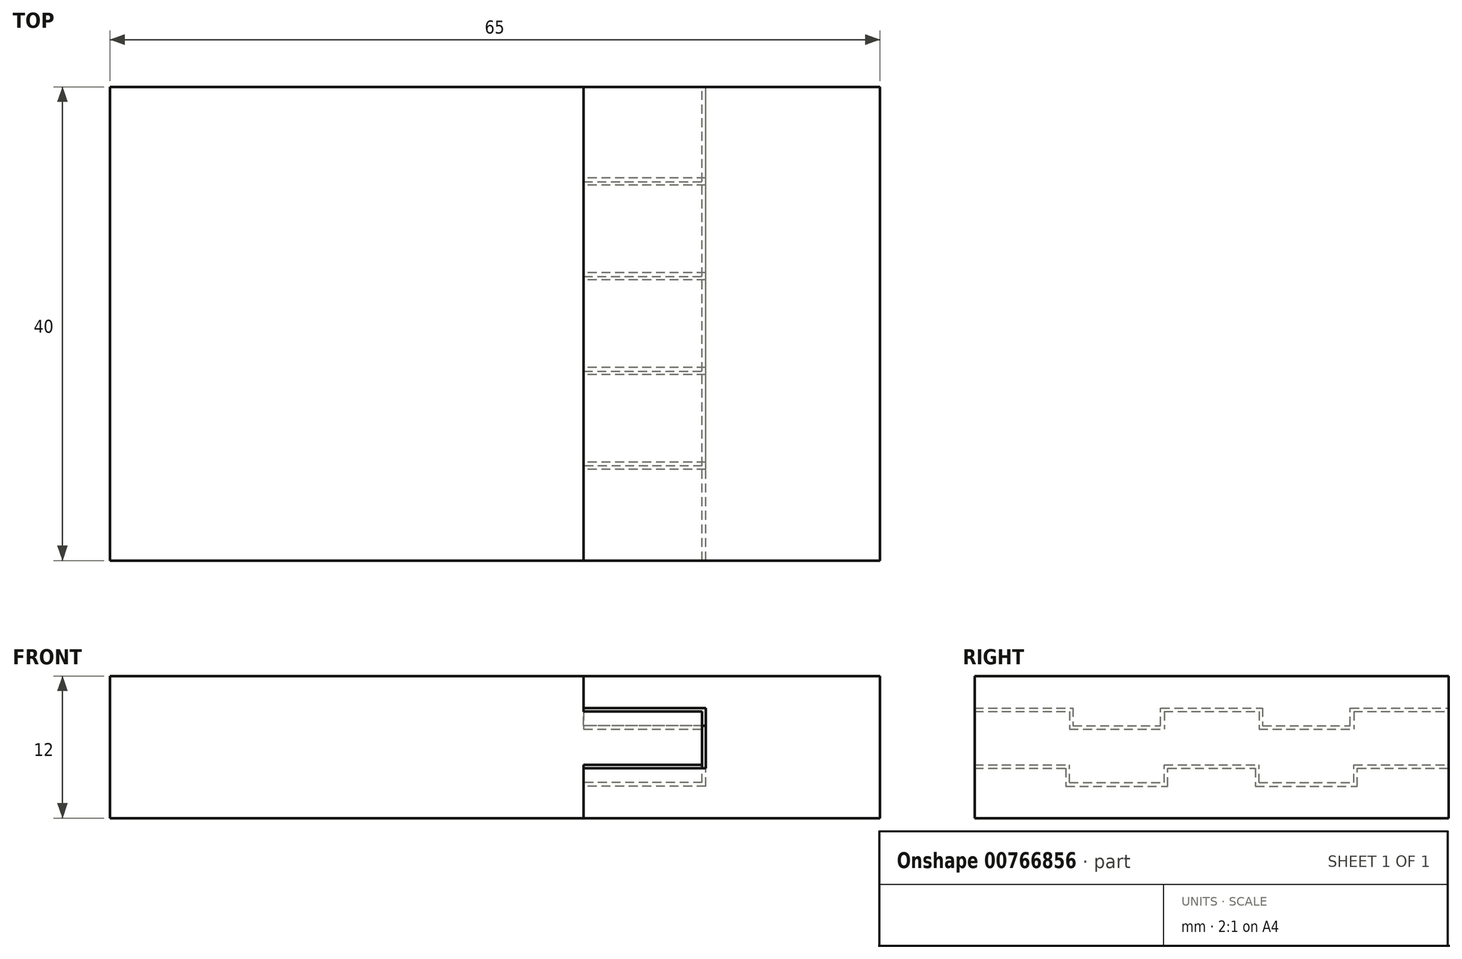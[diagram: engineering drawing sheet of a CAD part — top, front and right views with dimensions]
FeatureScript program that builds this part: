
annotation { "Feature Type Name" : "Feature", "Feature Type Description" : "" }
export const myFeature = defineFeature(function(context is Context, id is Id, definition is map)
    precondition{}
    {
        {
            var Q0;
            Q0=qCreatedBy(makeId("Top.planeOp"),FACE);
            var sketch = newSketch(context, id + "F0", { "sketchPlane" : qUnion([Q0])});
            skLineSegment(sketch, "E0.bottom", {"start": v(-40, 40) * mm, "end": v(0, 40) * mm});
            skLineSegment(sketch, "E0.top", {"start": v(-40, 0) * mm, "end": v(0, 0) * mm});
            skLineSegment(sketch, "E0.left", {"start": v(-40, 40) * mm, "end": v(-40, 0) * mm});
            skLineSegment(sketch, "E1", {"start": v(0, 0) * mm, "end": v(0, 40) * mm});
            skLineSegment(sketch, "E2.bottom", {"start": v(0, 0) * mm, "end": v(10, 0) * mm});
            skLineSegment(sketch, "E2.top", {"start": v(0, 8) * mm, "end": v(10, 8) * mm});
            skLineSegment(sketch, "E2.left", {"start": v(0, 0) * mm, "end": v(0, 8) * mm});
            skLineSegment(sketch, "E2.right", {"start": v(10, 0) * mm, "end": v(10, 8) * mm});
            skLineSegment(sketch, "E3.bottom", {"start": v(10, 8) * mm, "end": v(0, 8) * mm});
            skLineSegment(sketch, "E3.top", {"start": v(10, 16) * mm, "end": v(0, 16) * mm});
            skLineSegment(sketch, "E3.left", {"start": v(10, 8) * mm, "end": v(10, 16) * mm});
            skLineSegment(sketch, "E3.right", {"start": v(0, 8) * mm, "end": v(0, 16) * mm});
            skLineSegment(sketch, "E4.top", {"start": v(10, 24) * mm, "end": v(0, 24) * mm});
            skLineSegment(sketch, "E4.left", {"start": v(10, 16) * mm, "end": v(10, 24) * mm});
            skLineSegment(sketch, "E4.right", {"start": v(0, 16) * mm, "end": v(0, 24) * mm});
            skLineSegment(sketch, "E5.top", {"start": v(10, 32) * mm, "end": v(0, 32) * mm});
            skLineSegment(sketch, "E5.left", {"start": v(10, 24) * mm, "end": v(10, 32) * mm});
            skLineSegment(sketch, "E5.right", {"start": v(0, 24) * mm, "end": v(0, 32) * mm});
            skLineSegment(sketch, "E6.top", {"start": v(10, 40) * mm, "end": v(0, 40) * mm});
            skLineSegment(sketch, "E6.left", {"start": v(10, 32) * mm, "end": v(10, 40) * mm});
            skLineSegment(sketch, "E6.right", {"start": v(0, 32) * mm, "end": v(0, 40) * mm});
            skSolve(sketch);
        }
        {
            var Q0;
            {var subQ4=sQuery(id+"F0.wireOp",EDGE,"E0.bottom");Q0=makeQuery(id+"F0.imprint","IMPRINT",FACE,{"disambiguationData":[TD([[makeQuery(id+"F0.imprint","IMPRINT",EDGE,{"derivedFrom":subQ4}),-1.0]])]});}
            extrude(context, id + "F1", {"entities" : qUnion([Q0]), "endBound" : BoundingType.SYMMETRIC, "depth" : 12 * mm, "offsetDistance" : 25 * mm});
        }
        {
            var Q0;
            {var subQ0=sQuery(id+"F0.wireOp",EDGE,"E2.bottom");Q0=makeQuery(id+"F0.imprint","IMPRINT",FACE,{"disambiguationData":[TD([[makeQuery(id+"F0.imprint","IMPRINT",EDGE,{"derivedFrom":subQ0}),1.0]])]});}
            var Q1;
            {var subQ0=sQuery(id+"F0.wireOp",EDGE,"E3.top");Q1=makeQuery(id+"F0.imprint","IMPRINT",FACE,{"disambiguationData":[TD([[makeQuery(id+"F0.imprint","IMPRINT",EDGE,{"derivedFrom":subQ0}),-1.0]])]});}
            var Q2;
            {var subQ0=sQuery(id+"F0.wireOp",EDGE,"E2.top");Q2=makeQuery(id+"F0.imprint","IMPRINT",FACE,{"disambiguationData":[TD([[makeQuery(id+"F0.imprint","IMPRINT",EDGE,{"derivedFrom":subQ0}),1.0]])]});}
            var Q3;
            {var subQ0=sQuery(id+"F0.wireOp",EDGE,"E4.top");Q3=makeQuery(id+"F0.imprint","IMPRINT",FACE,{"disambiguationData":[TD([[makeQuery(id+"F0.imprint","IMPRINT",EDGE,{"derivedFrom":subQ0}),-1.0]])]});}
            var Q4;
            {var subQ2=sQuery(id+"F0.wireOp",EDGE,"E5.top");Q4=makeQuery(id+"F0.imprint","IMPRINT",FACE,{"disambiguationData":[TD([[makeQuery(id+"F0.imprint","IMPRINT",EDGE,{"derivedFrom":subQ2}),-1.0]])]});}
            extrude(context, id + "F2", {"entities" : qUnion([Q0, Q1, Q2, Q3, Q4]), "operationType" : NewBodyOperationType.ADD, "endBound" : BoundingType.SYMMETRIC, "depth" : 3 * mm, "offsetDistance" : 25 * mm});
        }
        {
            var Q0;
            {var subQ0=sQuery(id+"F0.wireOp",EDGE,"E2.bottom");Q0=makeQuery(id+"F0.imprint","IMPRINT",FACE,{"disambiguationData":[TD([[makeQuery(id+"F0.imprint","IMPRINT",EDGE,{"derivedFrom":subQ0}),1.0]])]});}
            var Q1;
            {var subQ0=sQuery(id+"F0.wireOp",EDGE,"E3.top");Q1=makeQuery(id+"F0.imprint","IMPRINT",FACE,{"disambiguationData":[TD([[makeQuery(id+"F0.imprint","IMPRINT",EDGE,{"derivedFrom":subQ0}),-1.0]])]});}
            var Q2;
            {var subQ2=sQuery(id+"F0.wireOp",EDGE,"E5.top");Q2=makeQuery(id+"F0.imprint","IMPRINT",FACE,{"disambiguationData":[TD([[makeQuery(id+"F0.imprint","IMPRINT",EDGE,{"derivedFrom":subQ2}),-1.0]])]});}
            extrude(context, id + "F3", {"entities" : qUnion([Q0, Q1, Q2]), "operationType" : NewBodyOperationType.ADD, "depth" : 3 * mm, "offsetDistance" : 25 * mm});
        }
        {
            var Q0;
            {var subQ0=sQuery(id+"F0.wireOp",EDGE,"E2.right");var subQ1=sQuery(id+"F0.wireOp",EDGE,"E6.left");var subQ2=sQuery(id+"F0.wireOp",EDGE,"E5.left");var subQ3=sQuery(id+"F0.wireOp",EDGE,"E4.left");var subQ4=sQuery(id+"F0.wireOp",EDGE,"E3.left");var subQ5=sQuery(id+"F0.wireOp",EDGE,"E1");Q0=makeQuery(id+"F3.boolean.opBoolean","SPLIT",FACE,{"disambiguationData":[TD([makeQuery(id+"F3.opExtrude","SWEPT_FACE",FACE,{"disambiguationData":[OSD([sQuery(id+"F0.wireOp",EDGE,"E2.top")])]})])],"derivedFrom":makeQuery(id+"F2.opExtrude","CAP_FACE",FACE,{"disambiguationData":[OSD([subQ5,sQuery(id+"F0.wireOp",EDGE,"E2.bottom"),subQ0,subQ4,subQ3,subQ2,sQuery(id+"F0.wireOp",EDGE,"E6.top"),subQ1])],"isStart":false})});}
            var Q1;
            {var subQ0=sQuery(id+"F0.wireOp",EDGE,"E2.right");var subQ1=sQuery(id+"F0.wireOp",EDGE,"E6.left");var subQ2=sQuery(id+"F0.wireOp",EDGE,"E5.left");var subQ3=sQuery(id+"F0.wireOp",EDGE,"E4.left");var subQ4=sQuery(id+"F0.wireOp",EDGE,"E3.left");var subQ5=sQuery(id+"F0.wireOp",EDGE,"E1");Q1=makeQuery(id+"F3.boolean.opBoolean","SPLIT",FACE,{"disambiguationData":[TD([makeQuery(id+"F3.opExtrude","SWEPT_FACE",FACE,{"disambiguationData":[OSD([sQuery(id+"F0.wireOp",EDGE,"E4.top")])]})])],"derivedFrom":makeQuery(id+"F2.opExtrude","CAP_FACE",FACE,{"disambiguationData":[OSD([subQ5,sQuery(id+"F0.wireOp",EDGE,"E2.bottom"),subQ0,subQ4,subQ3,subQ2,sQuery(id+"F0.wireOp",EDGE,"E6.top"),subQ1])],"isStart":false})});}
            extrude(context, id + "F4", {"entities" : qUnion([Q0, Q1]), "operationType" : NewBodyOperationType.ADD, "oppositeDirection" : true, "depth" : 4.5 * mm, "offsetDistance" : 25 * mm});
        }
        {
            var Q0;
            {var subQ2=sQuery(id+"F0.wireOp",EDGE,"E1");var subQ3=sQuery(id+"F0.wireOp",EDGE,"E0.top");var subQ4=sQuery(id+"F0.wireOp",EDGE,"E0.bottom");Q0=makeQuery(id+"F2.boolean.opBoolean","SPLIT",FACE,{"disambiguationData":[TD([makeQuery(id+"F1.opExtrude","CAP_FACE",FACE,{"disambiguationData":[OSD([subQ4,subQ3,sQuery(id+"F0.wireOp",EDGE,"E0.left"),subQ2])],"isStart":false})])],"derivedFrom":makeQuery(id+"F1.opExtrude","SWEPT_FACE",FACE,{"disambiguationData":[OSD([subQ2])]})});}
            var sketch = newSketch(context, id + "F5", { "sketchPlane" : qUnion([Q0])});
            skLineSegment(sketch, "E7.0.0", {"start": v(32, 1.5) * mm, "end": v(32, 3) * mm});
            skLineSegment(sketch, "E7.0.1", {"start": v(32, 3) * mm, "end": v(40, 3) * mm});
            skLineSegment(sketch, "E7.0.2", {"start": v(40, 3) * mm, "end": v(40, 6) * mm});
            skLineSegment(sketch, "E7.0.3", {"start": v(40, 6) * mm, "end": v(0, 6) * mm});
            skLineSegment(sketch, "E7.0.4", {"start": v(0, 6) * mm, "end": v(0, 3) * mm});
            skLineSegment(sketch, "E7.0.5", {"start": v(0, 3) * mm, "end": v(8, 3) * mm});
            skLineSegment(sketch, "E7.0.6", {"start": v(8, 3) * mm, "end": v(8, 1.5) * mm});
            skLineSegment(sketch, "E7.0.7", {"start": v(8, 1.5) * mm, "end": v(16, 1.5) * mm});
            skLineSegment(sketch, "E7.0.8", {"start": v(16, 1.5) * mm, "end": v(16, 3) * mm});
            skLineSegment(sketch, "E7.0.9", {"start": v(16, 3) * mm, "end": v(24, 3) * mm});
            skLineSegment(sketch, "E7.0.10", {"start": v(24, 3) * mm, "end": v(24, 1.5) * mm});
            skLineSegment(sketch, "E7.0.11", {"start": v(24, 1.5) * mm, "end": v(32, 1.5) * mm});
            skLineSegment(sketch, "E8.0.0", {"start": v(32, -1.5) * mm, "end": v(32, -3) * mm});
            skLineSegment(sketch, "E8.0.1", {"start": v(32, -3) * mm, "end": v(24, -3) * mm});
            skLineSegment(sketch, "E8.0.2", {"start": v(24, -3) * mm, "end": v(24, -1.5) * mm});
            skLineSegment(sketch, "E8.0.3", {"start": v(24, -1.5) * mm, "end": v(16, -1.5) * mm});
            skLineSegment(sketch, "E8.0.4", {"start": v(16, -1.5) * mm, "end": v(16, -3) * mm});
            skLineSegment(sketch, "E8.0.5", {"start": v(16, -3) * mm, "end": v(8, -3) * mm});
            skLineSegment(sketch, "E8.0.6", {"start": v(8, -3) * mm, "end": v(8, -1.5) * mm});
            skLineSegment(sketch, "E8.0.7", {"start": v(8, -1.5) * mm, "end": v(0, -1.5) * mm});
            skLineSegment(sketch, "E8.0.8", {"start": v(0, -1.5) * mm, "end": v(0, -6) * mm});
            skLineSegment(sketch, "E8.0.9", {"start": v(0, -6) * mm, "end": v(40, -6) * mm});
            skLineSegment(sketch, "E8.0.10", {"start": v(40, -6) * mm, "end": v(40, -1.5) * mm});
            skLineSegment(sketch, "E8.0.11", {"start": v(40, -1.5) * mm, "end": v(32, -1.5) * mm});
            skLineSegment(sketch, "E9", {"start": v(0, 3.3) * mm, "end": v(8.3, 3.3) * mm});
            skLineSegment(sketch, "E10", {"start": v(8.3, 3.3) * mm, "end": v(8.3, 1.8) * mm});
            skLineSegment(sketch, "E11", {"start": v(8.3, 1.8) * mm, "end": v(15.7, 1.8) * mm});
            skLineSegment(sketch, "E12", {"start": v(15.7, 1.8) * mm, "end": v(15.7, 3.3) * mm});
            skLineSegment(sketch, "E13", {"start": v(15.7, 3.3) * mm, "end": v(24.3, 3.3) * mm});
            skLineSegment(sketch, "E14", {"start": v(24.3, 3.3) * mm, "end": v(24.3, 1.8) * mm});
            skLineSegment(sketch, "E15", {"start": v(24.3, 1.8) * mm, "end": v(31.7, 1.8) * mm});
            skLineSegment(sketch, "E16", {"start": v(31.7, 1.8) * mm, "end": v(31.7, 3.3) * mm});
            skLineSegment(sketch, "E17", {"start": v(31.7, 3.3) * mm, "end": v(40, 3.3) * mm});
            skLineSegment(sketch, "E18", {"start": v(0, -1.8) * mm, "end": v(7.7, -1.8) * mm});
            skLineSegment(sketch, "E19", {"start": v(7.7, -1.8) * mm, "end": v(7.7, -3.3) * mm});
            skLineSegment(sketch, "E20", {"start": v(7.7, -3.3) * mm, "end": v(16.3, -3.3) * mm});
            skLineSegment(sketch, "E21", {"start": v(16.3, -3.3) * mm, "end": v(16.3, -1.8) * mm});
            skLineSegment(sketch, "E22", {"start": v(16.3, -1.8) * mm, "end": v(23.7, -1.8) * mm});
            skLineSegment(sketch, "E23", {"start": v(23.7, -1.8) * mm, "end": v(23.7, -3.3) * mm});
            skLineSegment(sketch, "E24", {"start": v(23.7, -3.3) * mm, "end": v(32.3, -3.3) * mm});
            skLineSegment(sketch, "E25", {"start": v(32.3, -3.3) * mm, "end": v(32.3, -1.8) * mm});
            skLineSegment(sketch, "E26", {"start": v(32.3, -1.8) * mm, "end": v(40, -1.8) * mm});
            skSolve(sketch);
        }
        {
            var Q0;
            {var subQ0=sQuery(id+"F5.wireOp",EDGE,"E7.0.3");Q0=makeQuery(id+"F5.imprint","IMPRINT",FACE,{"disambiguationData":[TD([[makeQuery(id+"F5.imprint","IMPRINT",EDGE,{"derivedFrom":subQ0}),-1.0]])]});}
            var Q1;
            {var subQ0=sQuery(id+"F5.wireOp",EDGE,"E8.0.9");Q1=makeQuery(id+"F5.imprint","IMPRINT",FACE,{"disambiguationData":[TD([[makeQuery(id+"F5.imprint","IMPRINT",EDGE,{"derivedFrom":subQ0}),1.0]])]});}
            extrude(context, id + "F6", {"entities" : qUnion([Q0, Q1]), "depth" : 25 * mm, "offsetDistance" : 25 * mm});
        }
        {
            var Q0;
            Q0=makeQuery(id+"F6.opExtrude","SWEPT_FACE",FACE,{"disambiguationData":[OSD([sQuery(id+"F5.wireOp",EDGE,"E8.0.8")])]});
            var sketch = newSketch(context, id + "F7", { "sketchPlane" : qUnion([Q0])});
            skLineSegment(sketch, "E27.bottom", {"start": v(25, -6) * mm, "end": v(10.3, -6) * mm});
            skLineSegment(sketch, "E27.top", {"start": v(25, 6) * mm, "end": v(10.3, 6) * mm});
            skLineSegment(sketch, "E27.left", {"start": v(25, -6) * mm, "end": v(25, 6) * mm});
            skLineSegment(sketch, "E27.right", {"start": v(10.3, -6) * mm, "end": v(10.3, 6) * mm});
            skSolve(sketch);
        }
        {
            var Q0;
            {var subQ0=sQuery(id+"F7.wireOp",EDGE,"E27.top");Q0=makeQuery(id+"F7.imprint","IMPRINT",FACE,{"disambiguationData":[TD([[makeQuery(id+"F7.imprint","IMPRINT",EDGE,{"derivedFrom":subQ0}),1.0]])]});}
            var Q1;
            {var subQ0=sQuery(id+"F7.wireOp",EDGE,"E27.bottom");Q1=makeQuery(id+"F7.imprint","IMPRINT",FACE,{"disambiguationData":[TD([[makeQuery(id+"F7.imprint","IMPRINT",EDGE,{"derivedFrom":subQ0}),-1.0]])]});}
            var Q2;
            Q2=makeQuery(id+"F6.opExtrude","SWEPT_FACE",FACE,{"disambiguationData":[OSD([sQuery(id+"F5.wireOp",EDGE,"E7.0.2")])]});
            extrude(context, id + "F8", {"entities" : qUnion([Q0, Q1]), "operationType" : NewBodyOperationType.ADD, "endBound" : BoundingType.UP_TO_SURFACE, "oppositeDirection" : true, "depth" : 25 * mm, "endBoundEntityFace" : qUnion([Q2]), "offsetDistance" : 25 * mm});
        }
    });
